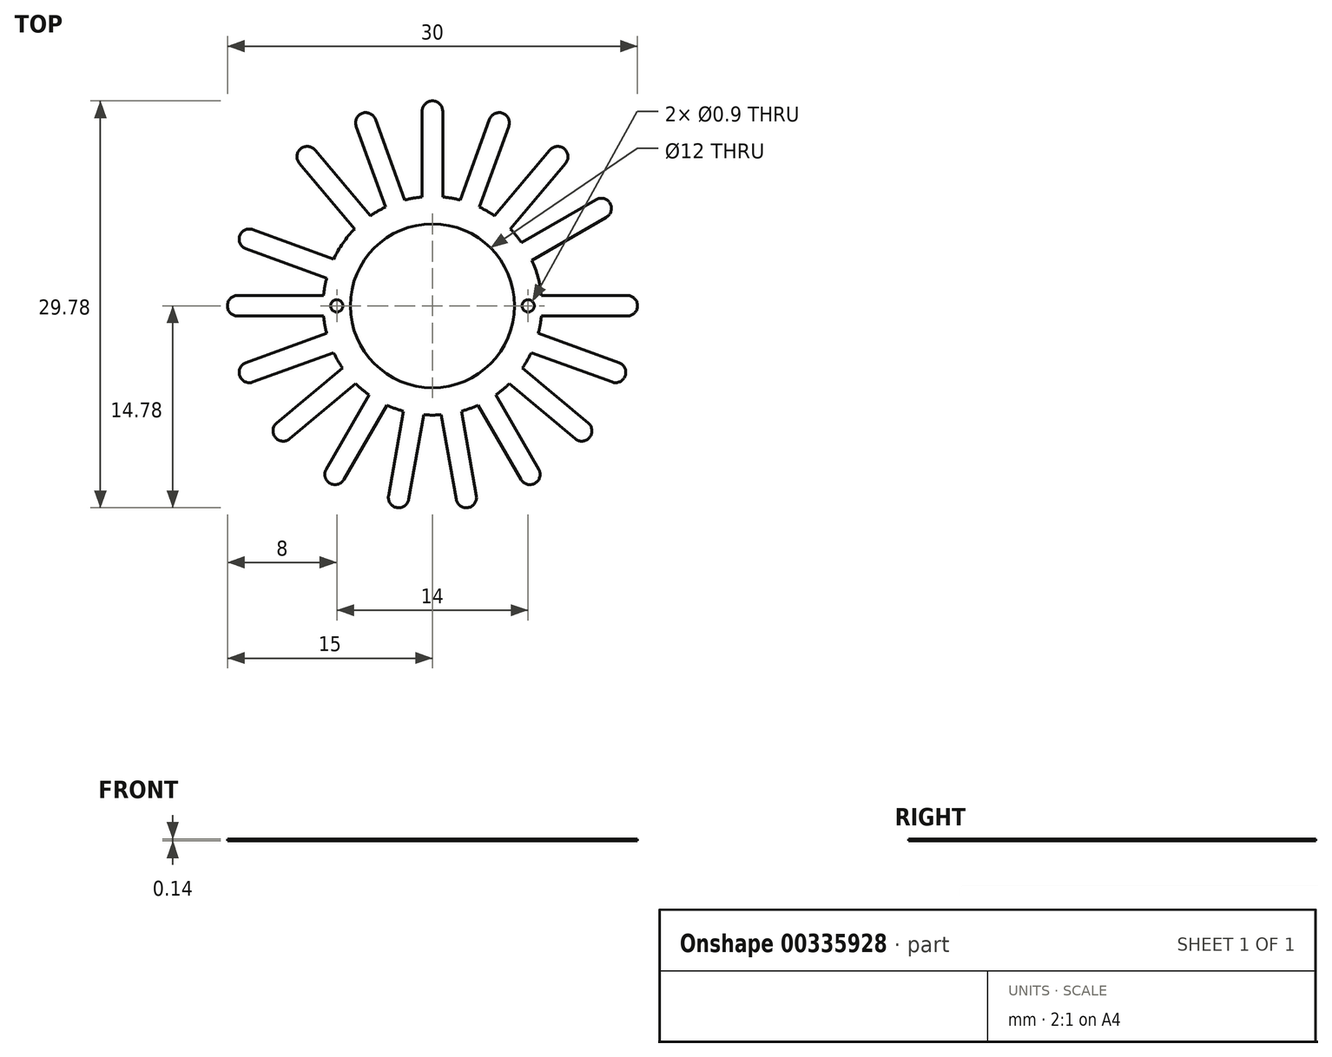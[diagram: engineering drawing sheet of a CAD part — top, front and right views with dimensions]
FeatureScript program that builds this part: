
annotation { "Feature Type Name" : "Feature", "Feature Type Description" : "" }
export const myFeature = defineFeature(function(context is Context, id is Id, definition is map)
    precondition{}
    {
        {
            var Q0;
            Q0=qCreatedBy(makeId("Top.planeOp"),FACE);
            var sketch = newSketch(context, id + "F0", { "sketchPlane" : qUnion([Q0])});
            skCircle(sketch, "E0", {"center": v(0, 0) * mm, "radius": 6 * mm});
            skCircle(sketch, "E1", {"center": v(0, 0) * mm, "radius": 8 * mm});
            skCircle(sketch, "E2", {"center": v(7, 0) * mm, "radius": 0.45 * mm});
            skCircle(sketch, "E3", {"center": v(-7, 0) * mm, "radius": 0.45 * mm});
            skLineSegment(sketch, "E4", {"start": v(-7, 0) * mm, "end": v(7, 0) * mm, "construction": true});
            skCircle(sketch, "E5", {"center": v(0, 0) * mm, "radius": 14.25 * mm, "construction": true});
            skLineSegment(sketch, "E6", {"start": v(0, 0) * mm, "end": v(14.25, 0) * mm, "construction": true});
            skArc(sketch, "E7", {"start": v(14.25, -0.75) * mm, "mid": v(15, 0) * mm, "end": v(14.25, 0.75) * mm});
            skLineSegment(sketch, "E8", {"start": v(14.25, 0.75) * mm, "end": v(7.96, 0.75) * mm});
            skLineSegment(sketch, "E9", {"start": v(14.25, -0.75) * mm, "end": v(7.96, -0.75) * mm});
            skLineSegment(sketch, "E10.1.0", {"start": v(13.65, -4.17) * mm, "end": v(7.74, -2.02) * mm});
            skArc(sketch, "E10.1.1", {"start": v(13.13, -5.58) * mm, "mid": v(14.1, -5.13) * mm, "end": v(13.65, -4.17) * mm});
            skLineSegment(sketch, "E10.1.2", {"start": v(13.13, -5.58) * mm, "end": v(7.23, -3.43) * mm});
            skLineSegment(sketch, "E10.2.0", {"start": v(11.4, -8.59) * mm, "end": v(6.58, -4.55) * mm});
            skArc(sketch, "E10.2.1", {"start": v(10.43, -9.73) * mm, "mid": v(11.5, -9.64) * mm, "end": v(11.4, -8.59) * mm});
            skLineSegment(sketch, "E10.2.2", {"start": v(10.43, -9.73) * mm, "end": v(5.62, -5.7) * mm});
            skLineSegment(sketch, "E10.3.0", {"start": v(7.77, -11.97) * mm, "end": v(4.63, -6.52) * mm});
            skArc(sketch, "E10.3.1", {"start": v(6.48, -12.72) * mm, "mid": v(7.5, -13) * mm, "end": v(7.77, -11.97) * mm});
            skLineSegment(sketch, "E10.3.2", {"start": v(6.48, -12.72) * mm, "end": v(3.33, -7.27) * mm});
            skLineSegment(sketch, "E10.4.0", {"start": v(3.21, -13.9) * mm, "end": v(2.12, -7.71) * mm});
            skArc(sketch, "E10.4.1", {"start": v(1.74, -14.16) * mm, "mid": v(2.6, -14.77) * mm, "end": v(3.21, -13.9) * mm});
            skLineSegment(sketch, "E10.4.2", {"start": v(1.74, -14.16) * mm, "end": v(0.64, -7.97) * mm});
            skLineSegment(sketch, "E10.5.0", {"start": v(-1.74, -14.16) * mm, "end": v(-0.64, -7.97) * mm});
            skArc(sketch, "E10.5.1", {"start": v(-3.21, -13.9) * mm, "mid": v(-2.6, -14.77) * mm, "end": v(-1.74, -14.16) * mm});
            skLineSegment(sketch, "E10.5.2", {"start": v(-3.21, -13.9) * mm, "end": v(-2.12, -7.71) * mm});
            skLineSegment(sketch, "E10.6.0", {"start": v(-6.48, -12.72) * mm, "end": v(-3.33, -7.27) * mm});
            skArc(sketch, "E10.6.1", {"start": v(-7.77, -11.97) * mm, "mid": v(-7.5, -13) * mm, "end": v(-6.48, -12.72) * mm});
            skLineSegment(sketch, "E10.6.2", {"start": v(-7.77, -11.97) * mm, "end": v(-4.63, -6.52) * mm});
            skLineSegment(sketch, "E10.7.0", {"start": v(-10.43, -9.73) * mm, "end": v(-5.62, -5.7) * mm});
            skArc(sketch, "E10.7.1", {"start": v(-11.4, -8.59) * mm, "mid": v(-11.5, -9.64) * mm, "end": v(-10.43, -9.73) * mm});
            skLineSegment(sketch, "E10.7.2", {"start": v(-11.4, -8.59) * mm, "end": v(-6.58, -4.55) * mm});
            skLineSegment(sketch, "E10.8.0", {"start": v(-13.13, -5.58) * mm, "end": v(-7.23, -3.43) * mm});
            skArc(sketch, "E10.8.1", {"start": v(-13.65, -4.17) * mm, "mid": v(-14.1, -5.13) * mm, "end": v(-13.13, -5.58) * mm});
            skLineSegment(sketch, "E10.8.2", {"start": v(-13.65, -4.17) * mm, "end": v(-7.74, -2.02) * mm});
            skLineSegment(sketch, "E10.9.0", {"start": v(-14.25, -0.75) * mm, "end": v(-7.96, -0.75) * mm});
            skArc(sketch, "E10.9.1", {"start": v(-14.25, 0.75) * mm, "mid": v(-15, 0) * mm, "end": v(-14.25, -0.75) * mm});
            skLineSegment(sketch, "E10.9.2", {"start": v(-14.25, 0.75) * mm, "end": v(-7.96, 0.75) * mm});
            skLineSegment(sketch, "E10.10.0", {"start": v(-13.65, 4.17) * mm, "end": v(-7.74, 2.02) * mm});
            skArc(sketch, "E10.10.1", {"start": v(-13.13, 5.58) * mm, "mid": v(-14.1, 5.13) * mm, "end": v(-13.65, 4.17) * mm});
            skLineSegment(sketch, "E10.10.2", {"start": v(-13.13, 5.58) * mm, "end": v(-7.23, 3.43) * mm});
            skLineSegment(sketch, "E10.anchor1", {"start": v(0, 0) * mm, "end": v(7.96, 0.75) * mm, "construction": true});
            skLineSegment(sketch, "E10.anchor2", {"start": v(0, 0) * mm, "end": v(-7.74, 2.02) * mm, "construction": true});
            skLineSegment(sketch, "E11", {"start": v(0, 0) * mm, "end": v(-9.16, 10.92) * mm, "construction": true});
            skArc(sketch, "E12", {"start": v(-9.73, 10.43) * mm, "mid": v(-9.64, 11.5) * mm, "end": v(-8.59, 11.4) * mm});
            skLineSegment(sketch, "E13", {"start": v(-5.7, 5.62) * mm, "end": v(-9.73, 10.43) * mm});
            skLineSegment(sketch, "E14", {"start": v(-4.55, 6.58) * mm, "end": v(-8.59, 11.4) * mm});
            skArc(sketch, "E15.1.0", {"start": v(-5.58, 13.13) * mm, "mid": v(-5.13, 14.1) * mm, "end": v(-4.17, 13.65) * mm});
            skLineSegment(sketch, "E15.1.1", {"start": v(-2.02, 7.74) * mm, "end": v(-4.17, 13.65) * mm});
            skLineSegment(sketch, "E15.1.2", {"start": v(-3.43, 7.23) * mm, "end": v(-5.58, 13.13) * mm});
            skArc(sketch, "E15.2.0", {"start": v(-0.75, 14.25) * mm, "mid": v(0, 15) * mm, "end": v(0.75, 14.25) * mm});
            skLineSegment(sketch, "E15.2.1", {"start": v(0.75, 7.96) * mm, "end": v(0.75, 14.25) * mm});
            skLineSegment(sketch, "E15.2.2", {"start": v(-0.75, 7.96) * mm, "end": v(-0.75, 14.25) * mm});
            skArc(sketch, "E15.3.0", {"start": v(4.17, 13.65) * mm, "mid": v(5.13, 14.1) * mm, "end": v(5.58, 13.13) * mm});
            skLineSegment(sketch, "E15.3.1", {"start": v(3.43, 7.23) * mm, "end": v(5.58, 13.13) * mm});
            skLineSegment(sketch, "E15.3.2", {"start": v(2.02, 7.74) * mm, "end": v(4.17, 13.65) * mm});
            skArc(sketch, "E15.4.0", {"start": v(8.59, 11.4) * mm, "mid": v(9.64, 11.5) * mm, "end": v(9.73, 10.43) * mm});
            skLineSegment(sketch, "E15.4.1", {"start": v(5.7, 5.62) * mm, "end": v(9.73, 10.43) * mm});
            skLineSegment(sketch, "E15.4.2", {"start": v(4.55, 6.58) * mm, "end": v(8.59, 11.4) * mm});
            skArc(sketch, "E15.5.0", {"start": v(11.97, 7.77) * mm, "mid": v(13, 7.5) * mm, "end": v(12.72, 6.48) * mm});
            skLineSegment(sketch, "E15.5.1", {"start": v(7.27, 3.33) * mm, "end": v(12.72, 6.48) * mm});
            skLineSegment(sketch, "E15.5.2", {"start": v(6.52, 4.63) * mm, "end": v(11.97, 7.77) * mm});
            skLineSegment(sketch, "E15.anchor1", {"start": v(0, 0) * mm, "end": v(-9.73, 10.43) * mm, "construction": true});
            skLineSegment(sketch, "E15.anchor2", {"start": v(0, 0) * mm, "end": v(11.97, 7.77) * mm, "construction": true});
            skSolve(sketch);
        }
        {
            var Q0;
            Q0 = qSketchRegion(id + "F0", true);
            extrude(context, id + "F1", {"entities" : qUnion([Q0]), "depth" : 0.14 * mm});
        }
    });
